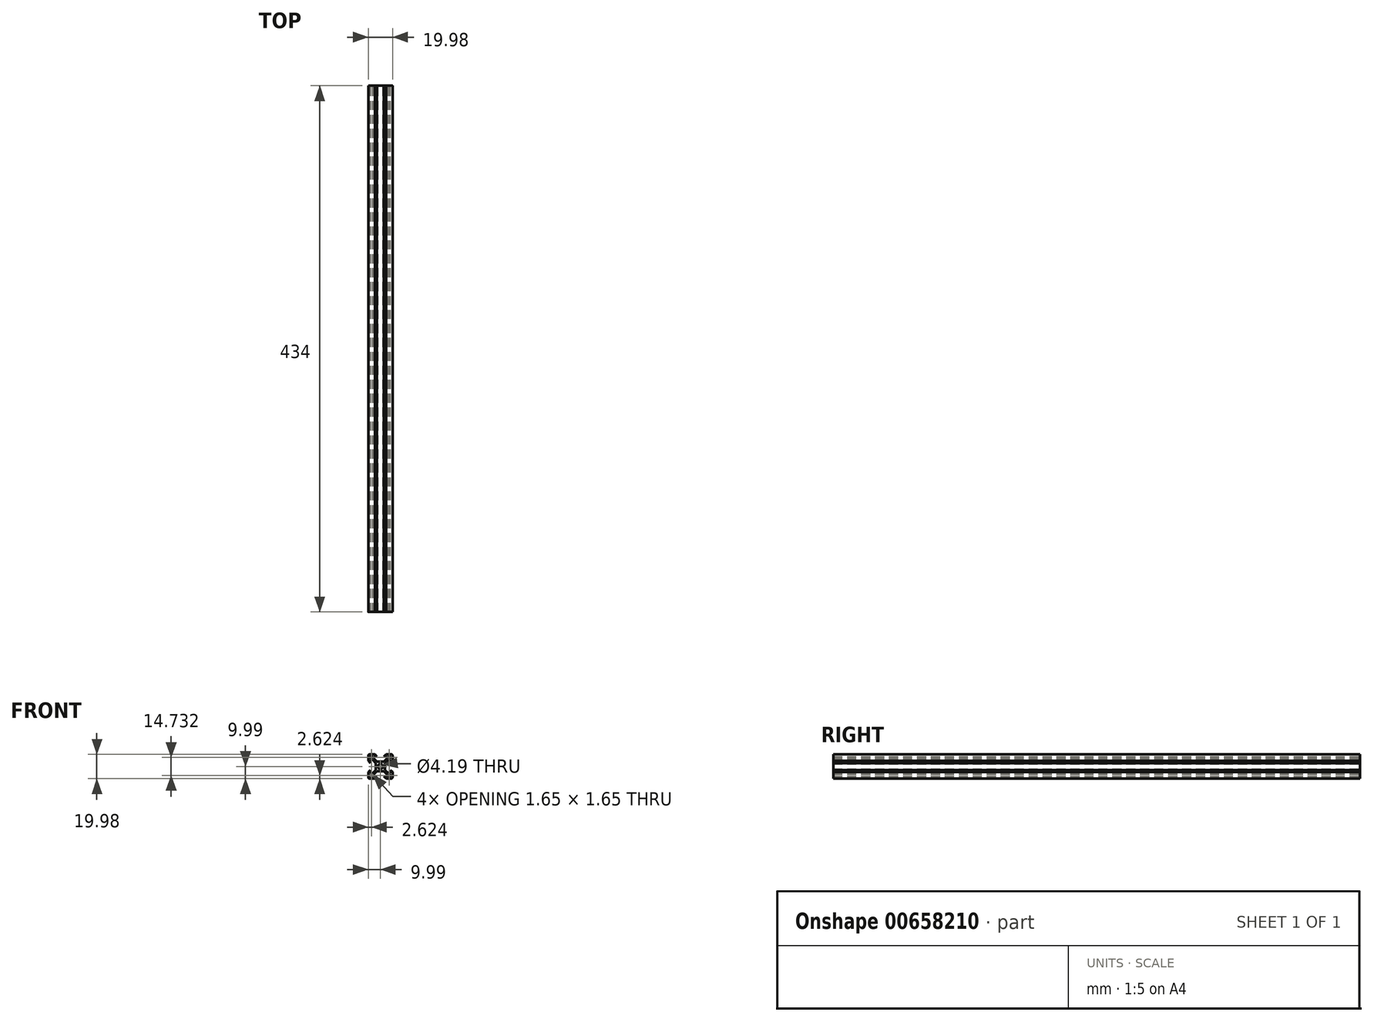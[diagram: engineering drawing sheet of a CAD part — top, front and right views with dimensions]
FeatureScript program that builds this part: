
annotation { "Feature Type Name" : "Feature", "Feature Type Description" : "" }
export const myFeature = defineFeature(function(context is Context, id is Id, definition is map)
    precondition{}
    {
        {
            var Q0;
            Q0=qCreatedBy(makeId("Front.planeOp"),FACE);
            var sketch = newSketch(context, id + "F0", { "sketchPlane" : qUnion([Q0])});
            skLineSegment(sketch, "E0.bottom", {"start": v(-9, 10) * mm, "end": v(-4.62, 10) * mm});
            skLineSegment(sketch, "E0.top", {"start": v(-9, -10) * mm, "end": v(-4.62, -10) * mm});
            skLineSegment(sketch, "E0.left", {"start": v(-10, 9) * mm, "end": v(-10, 4.62) * mm});
            skLineSegment(sketch, "E0.right", {"start": v(10, 9) * mm, "end": v(10, 4.62) * mm});
            skPoint(sketch, "E0.middle", {"position": v(0, 0) * mm});
            skPoint(sketch, "E1.visualSharp", {"position": v(10, 10) * mm});
            skArc(sketch, "E1.filletArc", {"start": v(10, 9) * mm, "mid": v(9.7, 9.7) * mm, "end": v(9, 10) * mm});
            skPoint(sketch, "E2.visualSharp", {"position": v(10, -10) * mm});
            skArc(sketch, "E2.filletArc", {"start": v(9, -10) * mm, "mid": v(9.7, -9.7) * mm, "end": v(10, -9) * mm});
            skPoint(sketch, "E3.visualSharp", {"position": v(-10, -10) * mm});
            skArc(sketch, "E3.filletArc", {"start": v(-10, -9) * mm, "mid": v(-9.7, -9.7) * mm, "end": v(-9, -10) * mm});
            skPoint(sketch, "E4.visualSharp", {"position": v(-10, 10) * mm});
            skArc(sketch, "E4.filletArc", {"start": v(-9, 10) * mm, "mid": v(-9.7, 9.7) * mm, "end": v(-10, 9) * mm});
            skCircle(sketch, "E5", {"center": v(0, 0) * mm, "radius": 2.1 * mm});
            skLineSegment(sketch, "E6.bottom", {"start": v(2.82, -3.9) * mm, "end": v(-2.82, -3.9) * mm});
            skLineSegment(sketch, "E6.top", {"start": v(2.82, 3.9) * mm, "end": v(-2.82, 3.9) * mm});
            skLineSegment(sketch, "E6.left", {"start": v(3.9, -2.82) * mm, "end": v(3.9, 2.82) * mm});
            skLineSegment(sketch, "E6.right", {"start": v(-3.9, -2.82) * mm, "end": v(-3.9, 2.82) * mm});
            skLineSegment(sketch, "E7.0", {"start": v(-6.54, 5.46) * mm, "end": v(-3.9, 2.82) * mm});
            skLineSegment(sketch, "E8.0", {"start": v(-5.46, 6.54) * mm, "end": v(-2.82, 3.9) * mm});
            skLineSegment(sketch, "E9.0", {"start": v(5.46, 6.54) * mm, "end": v(2.82, 3.9) * mm});
            skLineSegment(sketch, "E10.0", {"start": v(6.54, 5.46) * mm, "end": v(3.9, 2.82) * mm});
            skPoint(sketch, "E11.orphan", {"position": v(3.9, 3.9) * mm});
            skPoint(sketch, "E12.orphan", {"position": v(-3.9, 3.9) * mm});
            skPoint(sketch, "E13.orphan", {"position": v(-3.9, -3.9) * mm});
            skPoint(sketch, "E14.orphan", {"position": v(3.9, -3.9) * mm});
            skLineSegment(sketch, "E15.trimOffspring", {"start": v(3.9, -2.82) * mm, "end": v(6.54, -5.46) * mm});
            skLineSegment(sketch, "E16.trimOffspring", {"start": v(2.82, -3.9) * mm, "end": v(5.46, -6.54) * mm});
            skLineSegment(sketch, "E17.trimOffspring", {"start": v(-2.82, -3.9) * mm, "end": v(-5.46, -6.54) * mm});
            skLineSegment(sketch, "E18.trimOffspring", {"start": v(-3.9, -2.82) * mm, "end": v(-6.54, -5.46) * mm});
            skLineSegment(sketch, "E19", {"start": v(4.62, 10) * mm, "end": v(2.82, 8.2) * mm});
            skLineSegment(sketch, "E20", {"start": v(2.82, 8.2) * mm, "end": v(5.46, 8.2) * mm});
            skLineSegment(sketch, "E21", {"start": v(5.46, 8.2) * mm, "end": v(5.46, 6.54) * mm});
            skLineSegment(sketch, "E22.MirrorCS", {"start": v(-4.62, 10) * mm, "end": v(-2.82, 8.2) * mm});
            skLineSegment(sketch, "E23.MirrorCS", {"start": v(-2.82, 8.2) * mm, "end": v(-5.46, 8.2) * mm});
            skLineSegment(sketch, "E24.MirrorCS", {"start": v(-5.46, 8.2) * mm, "end": v(-5.46, 6.54) * mm});
            skLineSegment(sketch, "E25.MirrorCS", {"start": v(10, 4.62) * mm, "end": v(8.2, 2.82) * mm});
            skLineSegment(sketch, "E26.MirrorCS", {"start": v(8.2, 2.82) * mm, "end": v(8.2, 5.46) * mm});
            skLineSegment(sketch, "E27.MirrorCS", {"start": v(8.2, 5.46) * mm, "end": v(6.54, 5.46) * mm});
            skLineSegment(sketch, "E28.MirrorCS", {"start": v(-10, 4.62) * mm, "end": v(-8.2, 2.82) * mm});
            skLineSegment(sketch, "E29.MirrorCS", {"start": v(-8.2, 2.82) * mm, "end": v(-8.2, 5.46) * mm});
            skLineSegment(sketch, "E30.MirrorCS", {"start": v(-8.2, 5.46) * mm, "end": v(-6.54, 5.46) * mm});
            skLineSegment(sketch, "E31.MirrorCS", {"start": v(8.2, -5.46) * mm, "end": v(6.54, -5.46) * mm});
            skLineSegment(sketch, "E32.MirrorCS", {"start": v(8.2, -2.82) * mm, "end": v(8.2, -5.46) * mm});
            skLineSegment(sketch, "E33.MirrorCS", {"start": v(10, -4.62) * mm, "end": v(8.2, -2.82) * mm});
            skLineSegment(sketch, "E34.MirrorCS", {"start": v(-10, -4.62) * mm, "end": v(-8.2, -2.82) * mm});
            skLineSegment(sketch, "E35.MirrorCS", {"start": v(-8.2, -2.82) * mm, "end": v(-8.2, -5.46) * mm});
            skLineSegment(sketch, "E36.MirrorCS", {"start": v(-8.2, -5.46) * mm, "end": v(-6.54, -5.46) * mm});
            skLineSegment(sketch, "E37.MirrorCS", {"start": v(-5.46, -8.2) * mm, "end": v(-5.46, -6.54) * mm});
            skLineSegment(sketch, "E38.MirrorCS", {"start": v(-2.82, -8.2) * mm, "end": v(-5.46, -8.2) * mm});
            skLineSegment(sketch, "E39.MirrorCS", {"start": v(-4.62, -10) * mm, "end": v(-2.82, -8.2) * mm});
            skLineSegment(sketch, "E40.MirrorCS", {"start": v(4.62, -10) * mm, "end": v(2.82, -8.2) * mm});
            skLineSegment(sketch, "E41.MirrorCS", {"start": v(2.82, -8.2) * mm, "end": v(5.46, -8.2) * mm});
            skLineSegment(sketch, "E42.MirrorCS", {"start": v(5.46, -8.2) * mm, "end": v(5.46, -6.54) * mm});
            skLineSegment(sketch, "E43", {"start": v(-8.2, -8.04) * mm, "end": v(-8.2, -6.7) * mm});
            skLineSegment(sketch, "E44", {"start": v(-8.04, -8.2) * mm, "end": v(-6.7, -8.2) * mm});
            skLineSegment(sketch, "E45", {"start": v(-6.54, -8.04) * mm, "end": v(-6.54, -7.99) * mm});
            skLineSegment(sketch, "E46", {"start": v(-8.04, -6.54) * mm, "end": v(-7.99, -6.54) * mm});
            skLineSegment(sketch, "E47", {"start": v(-7.99, -6.54) * mm, "end": v(-6.54, -7.99) * mm});
            skPoint(sketch, "E48.visualSharp", {"position": v(-8.2, -8.2) * mm});
            skArc(sketch, "E48.filletArc", {"start": v(-8.2, -8.04) * mm, "mid": v(-8.15, -8.15) * mm, "end": v(-8.04, -8.2) * mm});
            skPoint(sketch, "E49.visualSharp", {"position": v(-6.54, -8.2) * mm});
            skArc(sketch, "E49.filletArc", {"start": v(-6.7, -8.2) * mm, "mid": v(-6.59, -8.15) * mm, "end": v(-6.54, -8.04) * mm});
            skPoint(sketch, "E50.visualSharp", {"position": v(-8.2, -6.54) * mm});
            skArc(sketch, "E50.filletArc", {"start": v(-8.04, -6.54) * mm, "mid": v(-8.15, -6.59) * mm, "end": v(-8.2, -6.7) * mm});
            skLineSegment(sketch, "E51.MirrorCS", {"start": v(8.2, -8.04) * mm, "end": v(8.2, -6.7) * mm});
            skArc(sketch, "E52.MirrorCS", {"start": v(8.2, -8.04) * mm, "mid": v(8.15, -8.15) * mm, "end": v(8.04, -8.2) * mm});
            skLineSegment(sketch, "E53.MirrorCS", {"start": v(8.04, -8.2) * mm, "end": v(6.7, -8.2) * mm});
            skArc(sketch, "E54.MirrorCS", {"start": v(6.7, -8.2) * mm, "mid": v(6.59, -8.15) * mm, "end": v(6.54, -8.04) * mm});
            skLineSegment(sketch, "E55.MirrorCS", {"start": v(6.54, -8.04) * mm, "end": v(6.54, -7.99) * mm});
            skLineSegment(sketch, "E56.MirrorCS", {"start": v(7.99, -6.54) * mm, "end": v(6.54, -7.99) * mm});
            skArc(sketch, "E57.MirrorCS", {"start": v(8.04, -6.54) * mm, "mid": v(8.15, -6.59) * mm, "end": v(8.2, -6.7) * mm});
            skLineSegment(sketch, "E58.MirrorCS", {"start": v(8.04, -6.54) * mm, "end": v(7.99, -6.54) * mm});
            skLineSegment(sketch, "E59.MirrorCS", {"start": v(8.04, 6.54) * mm, "end": v(7.99, 6.54) * mm});
            skLineSegment(sketch, "E60.MirrorCS", {"start": v(6.54, 8.04) * mm, "end": v(6.54, 7.99) * mm});
            skArc(sketch, "E61.MirrorCS", {"start": v(8.04, 6.54) * mm, "mid": v(8.15, 6.59) * mm, "end": v(8.2, 6.7) * mm});
            skArc(sketch, "E62.MirrorCS", {"start": v(6.7, 8.2) * mm, "mid": v(6.59, 8.15) * mm, "end": v(6.54, 8.04) * mm});
            skArc(sketch, "E63.MirrorCS", {"start": v(8.2, 8.04) * mm, "mid": v(8.15, 8.15) * mm, "end": v(8.04, 8.2) * mm});
            skLineSegment(sketch, "E64.MirrorCS", {"start": v(8.2, 8.04) * mm, "end": v(8.2, 6.7) * mm});
            skLineSegment(sketch, "E65.MirrorCS", {"start": v(8.04, 8.2) * mm, "end": v(6.7, 8.2) * mm});
            skLineSegment(sketch, "E66.MirrorCS", {"start": v(7.99, 6.54) * mm, "end": v(6.54, 7.99) * mm});
            skArc(sketch, "E67.MirrorCS", {"start": v(-8.04, 6.54) * mm, "mid": v(-8.15, 6.59) * mm, "end": v(-8.2, 6.7) * mm});
            skArc(sketch, "E68.MirrorCS", {"start": v(-6.7, 8.2) * mm, "mid": v(-6.59, 8.15) * mm, "end": v(-6.54, 8.04) * mm});
            skArc(sketch, "E69.MirrorCS", {"start": v(-8.2, 8.04) * mm, "mid": v(-8.15, 8.15) * mm, "end": v(-8.04, 8.2) * mm});
            skLineSegment(sketch, "E70.MirrorCS", {"start": v(-8.04, 6.54) * mm, "end": v(-7.99, 6.54) * mm});
            skLineSegment(sketch, "E71.MirrorCS", {"start": v(-6.54, 8.04) * mm, "end": v(-6.54, 7.99) * mm});
            skPoint(sketch, "E72.MirrorP", {"position": v(-8.2, 6.54) * mm});
            skPoint(sketch, "E73.MirrorP", {"position": v(-8.2, 8.2) * mm});
            skLineSegment(sketch, "E74.MirrorCS", {"start": v(-8.2, 8.04) * mm, "end": v(-8.2, 6.7) * mm});
            skLineSegment(sketch, "E75.MirrorCS", {"start": v(-7.99, 6.54) * mm, "end": v(-6.54, 7.99) * mm});
            skLineSegment(sketch, "E76.MirrorCS", {"start": v(-8.04, 8.2) * mm, "end": v(-6.7, 8.2) * mm});
            skPoint(sketch, "E77.MirrorP", {"position": v(-6.54, 8.2) * mm});
            skLineSegment(sketch, "E78.trimOffspring", {"start": v(10, -4.62) * mm, "end": v(10, -9) * mm});
            skLineSegment(sketch, "E79.trimOffspring", {"start": v(-10, -4.62) * mm, "end": v(-10, -9) * mm});
            skLineSegment(sketch, "E80.trimOffspring", {"start": v(4.62, -10) * mm, "end": v(9, -10) * mm});
            skLineSegment(sketch, "E81.trimOffspring", {"start": v(4.62, 10) * mm, "end": v(9, 10) * mm});
            skSolve(sketch);
        }
        {
            assignVariable(context, id + "F1", {"name" : "Length", "anyValue" : 434 * mm});
        }
        {
            var Q0;
            Q0=makeQuery(id+"F0.imprint","IMPRINT",FACE,{"disambiguationData":[TD([[makeQuery(id+"F0.imprint","IMPRINT",EDGE,{"derivedFrom":sQuery(id+"F0.wireOp",EDGE,"E0.bottom")}),-1.0]])]});
            extrude(context, id + "F2", {"entities" : qUnion([Q0]), "depth" : (getVariable(context, 'Length')), "offsetDistance" : 25.4 * mm});
        }
    });
